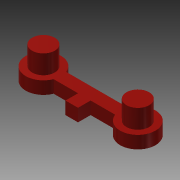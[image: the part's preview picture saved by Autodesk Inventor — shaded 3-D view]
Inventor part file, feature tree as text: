
AUTODESK INVENTOR PART (.ipt)
format: ipt  version: 2014 (Build 180170000, 170)  size: 100,864 bytes
history: native  units: mm
features: extrude x2, sketch x2, other x1
ambient origin geometry x8: Origin, YZ Plane, XZ Plane, XY Plane, X Axis, Y Axis, Z Axis, Center Point
bodies: Body1 (feature_tree)
feature tree (5):
  other  "Твердое тело1"
  extrude  "Выдавливание1"  Depth=5.6mm
  extrude  "Выдавливание2"  Depth=5.6mm
  sketch  "Эскиз1"
  sketch  "Эскиз2"
